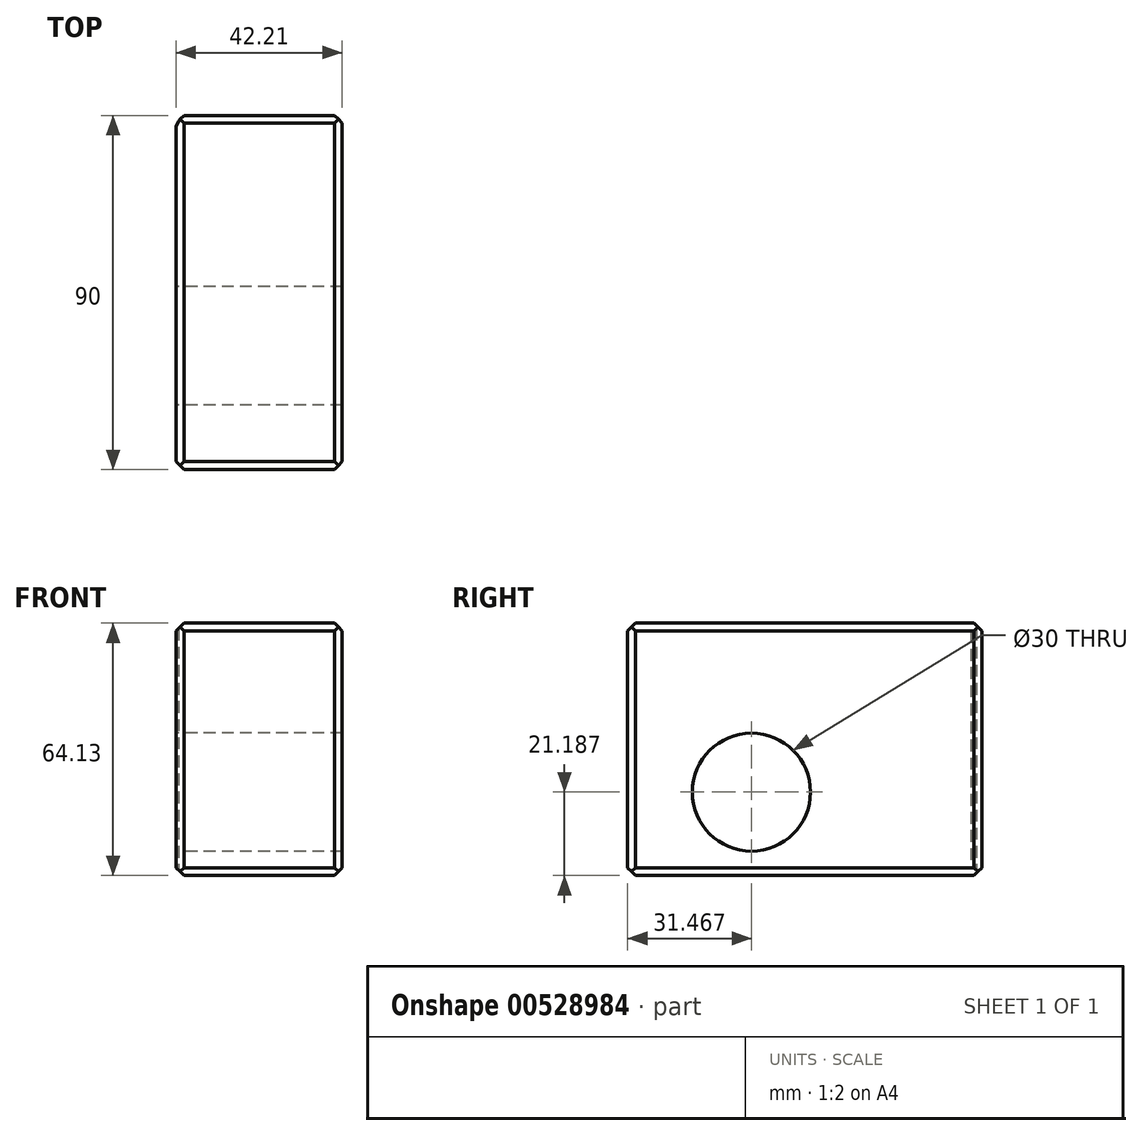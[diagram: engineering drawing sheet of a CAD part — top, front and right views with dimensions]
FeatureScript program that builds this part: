
annotation { "Feature Type Name" : "Feature", "Feature Type Description" : "" }
export const myFeature = defineFeature(function(context is Context, id is Id, definition is map)
    precondition{}
    {
        {
            var Q0;
            Q0=qCreatedBy(makeId("Front.planeOp"),FACE);
            var sketch = newSketch(context, id + "F0", { "sketchPlane" : qUnion([Q0])});
            skLineSegment(sketch, "E0.bottom", {"start": v(64.56, -37.73) * mm, "end": v(22.35, -37.73) * mm});
            skLineSegment(sketch, "E0.top", {"start": v(64.56, 26.4) * mm, "end": v(22.35, 26.4) * mm});
            skLineSegment(sketch, "E0.left", {"start": v(64.56, -37.73) * mm, "end": v(64.56, 26.4) * mm});
            skLineSegment(sketch, "E0.right", {"start": v(22.35, -37.73) * mm, "end": v(22.35, 26.4) * mm});
            skSolve(sketch);
        }
        {
            var Q0;
            Q0=makeQuery(id+"F0.imprint","IMPRINT",FACE,{"disambiguationData":[TD([[makeQuery(id+"F0.imprint","IMPRINT",EDGE,{"derivedFrom":sQuery(id+"F0.wireOp",EDGE,"E0.bottom")}),-1.0]])]});
            extrude(context, id + "F1", {"entities" : qUnion([Q0]), "oppositeDirection" : true, "depth" : 90 * mm, "offsetDistance" : 25 * mm});
        }
        {
            var Q0;
            Q0=makeQuery(id+"F1.opExtrude","CAP_EDGE",EDGE,{"disambiguationData":[OSD([sQuery(id+"F0.wireOp",EDGE,"E0.bottom")])],"isStart":true});
            var Q1;
            Q1=makeQuery(id+"F1.opExtrude","CAP_EDGE",EDGE,{"disambiguationData":[OSD([sQuery(id+"F0.wireOp",EDGE,"E0.left")])],"isStart":true});
            chamfer(context, id + "F2", {"entities" : qUnion([Q0, Q1]), "chamferType" : ChamferType.TWO_OFFSETS, "width1" : 2 * mm, "oppositeDirection" : false, "width2" : 2 * mm, "tangentPropagation" : true});
        }
        {
            var Q0;
            Q0=makeQuery(id+"F1.opExtrude","SWEPT_EDGE",EDGE,{"disambiguationData":[OSD([sQuery(id+"F0.wireOp",EDGE,"E0.bottom"),sQuery(id+"F0.wireOp",EDGE,"E0.left")])]});
            var Q1;
            Q1=makeQuery(id+"F1.opExtrude","SWEPT_EDGE",EDGE,{"disambiguationData":[OSD([sQuery(id+"F0.wireOp",EDGE,"E0.bottom"),sQuery(id+"F0.wireOp",EDGE,"E0.right")])]});
            var Q2;
            Q2=makeQuery(id+"F1.opExtrude","CAP_EDGE",EDGE,{"disambiguationData":[OSD([sQuery(id+"F0.wireOp",EDGE,"E0.bottom")])],"isStart":false});
            chamfer(context, id + "F3", {"entities" : qUnion([Q0, Q1, Q2]), "chamferType" : ChamferType.TWO_OFFSETS, "width1" : 2 * mm, "oppositeDirection" : false, "width2" : 2 * mm, "tangentPropagation" : true});
        }
        {
            var Q0;
            Q0=makeQuery(id+"F1.opExtrude","CAP_EDGE",EDGE,{"disambiguationData":[OSD([sQuery(id+"F0.wireOp",EDGE,"E0.left")])],"isStart":false});
            var Q1;
            Q1=makeQuery(id+"F1.opExtrude","CAP_EDGE",EDGE,{"disambiguationData":[OSD([sQuery(id+"F0.wireOp",EDGE,"E0.right")])],"isStart":false});
            var Q2;
            Q2=makeQuery(id+"F1.opExtrude","CAP_EDGE",EDGE,{"disambiguationData":[OSD([sQuery(id+"F0.wireOp",EDGE,"E0.top")])],"isStart":false});
            chamfer(context, id + "F4", {"entities" : qUnion([Q0, Q1, Q2]), "width" : 2 * mm, "tangentPropagation" : true});
        }
        {
            var Q0;
            Q0=makeQuery(id+"F1.opExtrude","CAP_EDGE",EDGE,{"disambiguationData":[OSD([sQuery(id+"F0.wireOp",EDGE,"E0.right")])],"isStart":true});
            var Q1;
            Q1=makeQuery(id+"F1.opExtrude","SWEPT_EDGE",EDGE,{"disambiguationData":[OSD([sQuery(id+"F0.wireOp",EDGE,"E0.top"),sQuery(id+"F0.wireOp",EDGE,"E0.right")])]});
            var Q2;
            {var subQ0=sQuery(id+"F0.wireOp",EDGE,"E0.right");Q2=makeQuery(id+"F4.opChamfer","BLEND_EDGE",EDGE,{"blendedFrom":[makeQuery(id+"F1.opExtrude","CAP_EDGE",EDGE,{"disambiguationData":[OSD([subQ0])],"isStart":false}),makeQuery(id+"F1.opExtrude","SWEPT_FACE",FACE,{"disambiguationData":[OSD([subQ0])]})],"blendedInto":[makeQuery(id+"F1.opExtrude","SWEPT_FACE",FACE,{"disambiguationData":[OSD([subQ0])]})]});}
            chamfer(context, id + "F5", {"entities" : qUnion([Q0, Q1, Q2]), "width" : 2 * mm, "tangentPropagation" : true});
        }
        {
            var Q0;
            Q0=makeQuery(id+"F1.opExtrude","SWEPT_EDGE",EDGE,{"disambiguationData":[OSD([sQuery(id+"F0.wireOp",EDGE,"E0.top"),sQuery(id+"F0.wireOp",EDGE,"E0.left")])]});
            var Q1;
            Q1=makeQuery(id+"F1.opExtrude","CAP_EDGE",EDGE,{"disambiguationData":[OSD([sQuery(id+"F0.wireOp",EDGE,"E0.top")])],"isStart":true});
            chamfer(context, id + "F6", {"entities" : qUnion([Q0, Q1]), "width" : 2 * mm, "tangentPropagation" : true});
        }
        {
            var Q0;
            Q0=makeQuery(id+"F1.opExtrude","SWEPT_FACE",FACE,{"disambiguationData":[OSD([sQuery(id+"F0.wireOp",EDGE,"E0.right")])]});
            var sketch = newSketch(context, id + "F7", { "sketchPlane" : qUnion([Q0])});
            skCircle(sketch, "E1", {"center": v(-31.47, -16.54) * mm, "radius": 10.24 * mm});
            skSolve(sketch);
        }
        {
            var Q0;
            Q0=sQuery(id+"F7.wireOp",VERTEX,"E1.center");
            var Q1;
            Q1=makeQuery(id+"F1.opExtrude","SWEPT_BODY",BODY,{"disambiguationData":[OSD([sQuery(id+"F0.wireOp",EDGE,"E0.bottom"),sQuery(id+"F0.wireOp",EDGE,"E0.top"),sQuery(id+"F0.wireOp",EDGE,"E0.left"),sQuery(id+"F0.wireOp",EDGE,"E0.right")])]});
            hole(context, id + "F8", {"style" : HoleStyle.C_SINK, "endStyle" : HoleEndStyle.THROUGH, "holeDiameter" : 30 * mm, "cSinkDiameter" : 30 * mm, "cSinkAngle" : 45 * degree, "isTappedThrough" : true, "tappedDepth" : 12 * mm, "tapClearance" : 3, "startFromSketch" : true, "locations" : qUnion([Q0]), "scope" : qUnion([Q1])});
        }
    });
